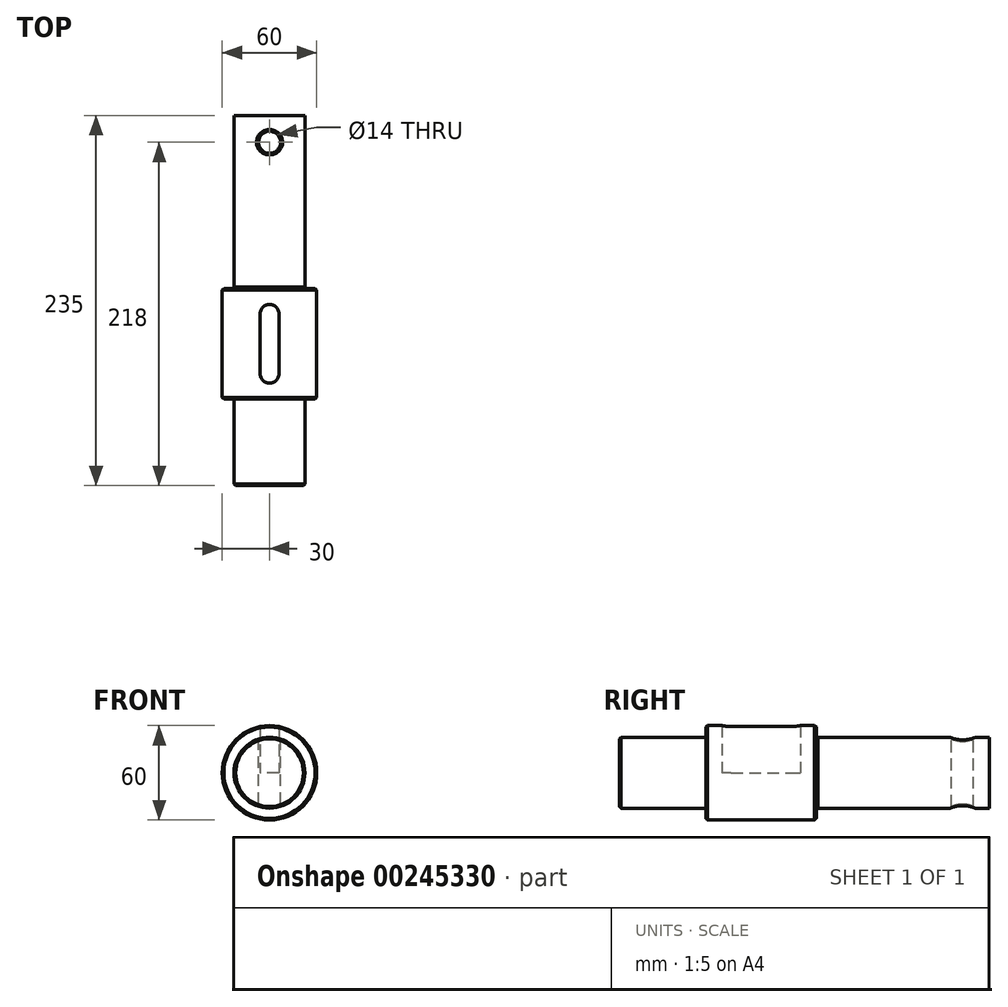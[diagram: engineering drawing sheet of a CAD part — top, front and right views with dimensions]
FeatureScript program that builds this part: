
annotation { "Feature Type Name" : "Feature", "Feature Type Description" : "" }
export const myFeature = defineFeature(function(context is Context, id is Id, definition is map)
    precondition{}
    {
        {
            var Q0;
            Q0=qCreatedBy(makeId("Front.planeOp"),FACE);
            var sketch = newSketch(context, id + "F0", { "sketchPlane" : qUnion([Q0])});
            skCircle(sketch, "E0", {"center": v(0, 0) * mm, "radius": 22.5 * mm});
            skSolve(sketch);
        }
        {
            var Q0;
            Q0 = qSketchRegion(id + "F0", true);
            extrude(context, id + "F1", {"entities" : qUnion([Q0]), "depth" : 110 * mm, "offsetDistance" : 25 * mm});
        }
        {
            var Q0;
            Q0=qCreatedBy(makeId("Top.planeOp"),FACE);
            var sketch = newSketch(context, id + "F2", { "sketchPlane" : qUnion([Q0])});
            skCircle(sketch, "E1", {"center": v(0, -17) * mm, "radius": 7 * mm});
            skSolve(sketch);
        }
        {
            var Q0;
            Q0 = qSketchRegion(id + "F2", true);
            extrude(context, id + "F3", {"entities" : qUnion([Q0]), "operationType" : NewBodyOperationType.REMOVE, "endBound" : BoundingType.THROUGH_ALL, "oppositeDirection" : true, "depth" : 25 * mm, "offsetDistance" : 25 * mm, "hasSecondDirection" : true, "secondDirectionBound" : SecondDirectionBoundingType.THROUGH_ALL, "secondDirectionOppositeDirection" : false, "secondDirectionDepth" : 25 * mm});
        }
        {
            var Q0;
            Q0=makeQuery(id+"F3.boolean.opBoolean","INTERSECT",EDGE,{"disambiguationData":[OD(0.0)],"derivedFrom":[makeQuery(id+"F1.opExtrude","SWEPT_FACE",FACE,{"disambiguationData":[OSD([sQuery(id+"F0.wireOp",EDGE,"E0")])]}),makeQuery(id+"F3.opExtrude","SWEPT_FACE",FACE,{"disambiguationData":[OSD([sQuery(id+"F2.wireOp",EDGE,"E1")])]})]});
            var Q1;
            Q1=makeQuery(id+"F3.boolean.opBoolean","INTERSECT",EDGE,{"disambiguationData":[OD(1.0)],"derivedFrom":[makeQuery(id+"F1.opExtrude","SWEPT_FACE",FACE,{"disambiguationData":[OSD([sQuery(id+"F0.wireOp",EDGE,"E0")])]}),makeQuery(id+"F3.opExtrude","SWEPT_FACE",FACE,{"disambiguationData":[OSD([sQuery(id+"F2.wireOp",EDGE,"E1")])]})]});
            var Q2;
            Q2=makeQuery(id+"FgVqdPoODl7SCyA_1.boolean.opBoolean","INTERSECT",EDGE,{"disambiguationData":[OD(1.0)],"derivedFrom":[makeQuery(id+"F1.opExtrude","SWEPT_FACE",FACE,{"disambiguationData":[OSD([sQuery(id+"F0.wireOp",EDGE,"E0")])]}),makeQuery(id+"FgVqdPoODl7SCyA_1.opExtrude","SWEPT_FACE",FACE,{"disambiguationData":[OSD([sQuery(id+"FY2ivZKtXJa3WG1_1.wireOp",EDGE,"Hc0Fqwav-KuhF-CdOD-GJRH-0QC76LvEiqeI.top")])]})]});
            var Q3;
            Q3=makeQuery(id+"FgVqdPoODl7SCyA_1.boolean.opBoolean","INTERSECT",EDGE,{"disambiguationData":[OD(1.0)],"derivedFrom":[makeQuery(id+"F1.opExtrude","SWEPT_FACE",FACE,{"disambiguationData":[OSD([sQuery(id+"F0.wireOp",EDGE,"E0")])]}),makeQuery(id+"FgVqdPoODl7SCyA_1.opExtrude","SWEPT_FACE",FACE,{"disambiguationData":[OSD([sQuery(id+"FY2ivZKtXJa3WG1_1.wireOp",EDGE,"Hc0Fqwav-KuhF-CdOD-GJRH-0QC76LvEiqeI.bottom")])]})]});
            var Q4;
            Q4=makeQuery(id+"FgVqdPoODl7SCyA_1.boolean.opBoolean","INTERSECT",EDGE,{"disambiguationData":[OD(1.0)],"derivedFrom":[makeQuery(id+"F1.opExtrude","SWEPT_FACE",FACE,{"disambiguationData":[OSD([sQuery(id+"F0.wireOp",EDGE,"E0")])]}),makeQuery(id+"FgVqdPoODl7SCyA_1.opExtrude","CAP_FACE",FACE,{"disambiguationData":[OSD([sQuery(id+"FY2ivZKtXJa3WG1_1.wireOp",EDGE,"Hc0Fqwav-KuhF-CdOD-GJRH-0QC76LvEiqeI.bottom"),sQuery(id+"FY2ivZKtXJa3WG1_1.wireOp",EDGE,"Hc0Fqwav-KuhF-CdOD-GJRH-0QC76LvEiqeI.top"),sQuery(id+"FY2ivZKtXJa3WG1_1.wireOp",EDGE,"Hc0Fqwav-KuhF-CdOD-GJRH-0QC76LvEiqeI.left"),sQuery(id+"FY2ivZKtXJa3WG1_1.wireOp",EDGE,"Hc0Fqwav-KuhF-CdOD-GJRH-0QC76LvEiqeI.right")])],"isStart":false})]});
            var Q5;
            Q5=makeQuery(id+"FgVqdPoODl7SCyA_1.boolean.opBoolean","COPY",EDGE,{"derivedFrom":makeQuery(id+"FgVqdPoODl7SCyA_1.opExtrude","CAP_EDGE",EDGE,{"disambiguationData":[OSD([sQuery(id+"FY2ivZKtXJa3WG1_1.wireOp",EDGE,"Hc0Fqwav-KuhF-CdOD-GJRH-0QC76LvEiqeI.bottom")])],"isStart":true})});
            var Q6;
            Q6=makeQuery(id+"FgVqdPoODl7SCyA_1.boolean.opBoolean","COPY",EDGE,{"derivedFrom":makeQuery(id+"FgVqdPoODl7SCyA_1.opExtrude","CAP_EDGE",EDGE,{"disambiguationData":[OSD([sQuery(id+"FY2ivZKtXJa3WG1_1.wireOp",EDGE,"Hc0Fqwav-KuhF-CdOD-GJRH-0QC76LvEiqeI.top")])],"isStart":true})});
            var Q7;
            Q7=makeQuery(id+"FgVqdPoODl7SCyA_1.boolean.opBoolean","INTERSECT",EDGE,{"disambiguationData":[OD(0.0)],"derivedFrom":[makeQuery(id+"F1.opExtrude","SWEPT_FACE",FACE,{"disambiguationData":[OSD([sQuery(id+"F0.wireOp",EDGE,"E0")])]}),makeQuery(id+"FgVqdPoODl7SCyA_1.opExtrude","SWEPT_FACE",FACE,{"disambiguationData":[OSD([sQuery(id+"FY2ivZKtXJa3WG1_1.wireOp",EDGE,"Hc0Fqwav-KuhF-CdOD-GJRH-0QC76LvEiqeI.top")])]})]});
            var Q8;
            Q8=makeQuery(id+"FgVqdPoODl7SCyA_1.boolean.opBoolean","INTERSECT",EDGE,{"disambiguationData":[OD(0.0)],"derivedFrom":[makeQuery(id+"F1.opExtrude","SWEPT_FACE",FACE,{"disambiguationData":[OSD([sQuery(id+"F0.wireOp",EDGE,"E0")])]}),makeQuery(id+"FgVqdPoODl7SCyA_1.opExtrude","SWEPT_FACE",FACE,{"disambiguationData":[OSD([sQuery(id+"FY2ivZKtXJa3WG1_1.wireOp",EDGE,"Hc0Fqwav-KuhF-CdOD-GJRH-0QC76LvEiqeI.bottom")])]})]});
            var Q9;
            Q9=makeQuery(id+"FgVqdPoODl7SCyA_1.boolean.opBoolean","INTERSECT",EDGE,{"disambiguationData":[OD(0.0)],"derivedFrom":[makeQuery(id+"F1.opExtrude","SWEPT_FACE",FACE,{"disambiguationData":[OSD([sQuery(id+"F0.wireOp",EDGE,"E0")])]}),makeQuery(id+"FgVqdPoODl7SCyA_1.opExtrude","CAP_FACE",FACE,{"disambiguationData":[OSD([sQuery(id+"FY2ivZKtXJa3WG1_1.wireOp",EDGE,"Hc0Fqwav-KuhF-CdOD-GJRH-0QC76LvEiqeI.bottom"),sQuery(id+"FY2ivZKtXJa3WG1_1.wireOp",EDGE,"Hc0Fqwav-KuhF-CdOD-GJRH-0QC76LvEiqeI.top"),sQuery(id+"FY2ivZKtXJa3WG1_1.wireOp",EDGE,"Hc0Fqwav-KuhF-CdOD-GJRH-0QC76LvEiqeI.left"),sQuery(id+"FY2ivZKtXJa3WG1_1.wireOp",EDGE,"Hc0Fqwav-KuhF-CdOD-GJRH-0QC76LvEiqeI.right")])],"isStart":false})]});
            chamfer(context, id + "F4", {"entities" : qUnion([Q0, Q1, Q2, Q3, Q4, Q5, Q6, Q7, Q8, Q9]), "width" : 1 * mm, "tangentPropagation" : true});
        }
        {
            var Q0;
            Q0=makeQuery(id+"F1.opExtrude","CAP_EDGE",EDGE,{"disambiguationData":[OSD([sQuery(id+"F0.wireOp",EDGE,"E0")])],"isStart":false});
            chamfer(context, id + "F5", {"entities" : qUnion([Q0]), "width" : 1 * mm, "tangentPropagation" : true});
        }
        {
            var Q0;
            Q0=makeQuery(id+"F1.opExtrude","CAP_FACE",FACE,{"disambiguationData":[OSD([sQuery(id+"F0.wireOp",EDGE,"E0")])],"isStart":false});
            var sketch = newSketch(context, id + "F6", { "sketchPlane" : qUnion([Q0])});
            skCircle(sketch, "E2", {"center": v(0, 0) * mm, "radius": 30 * mm});
            skSolve(sketch);
        }
        {
            var Q0;
            Q0 = qSketchRegion(id + "F6", true);
            extrude(context, id + "F7", {"entities" : qUnion([Q0]), "operationType" : NewBodyOperationType.ADD, "depth" : 70 * mm, "offsetDistance" : 25 * mm});
        }
        {
            var Q0;
            Q0=makeQuery(id+"F7.opExtrude","CAP_FACE",FACE,{"disambiguationData":[OSD([sQuery(id+"F6.wireOp",EDGE,"E2")])],"isStart":false});
            var sketch = newSketch(context, id + "F8", { "sketchPlane" : qUnion([Q0])});
            skCircle(sketch, "E3", {"center": v(0, 0) * mm, "radius": 22.5 * mm});
            skSolve(sketch);
        }
        {
            var Q0;
            Q0 = qSketchRegion(id + "F8", true);
            extrude(context, id + "F9", {"entities" : qUnion([Q0]), "operationType" : NewBodyOperationType.ADD, "depth" : 55 * mm, "offsetDistance" : 25 * mm});
        }
        {
            var Q0;
            Q0=makeQuery(id+"F9.opExtrude","CAP_EDGE",EDGE,{"disambiguationData":[OSD([sQuery(id+"F8.wireOp",EDGE,"E3")])],"isStart":false});
            var Q1;
            Q1=makeQuery(id+"F7.opExtrude","CAP_EDGE",EDGE,{"disambiguationData":[OSD([sQuery(id+"F6.wireOp",EDGE,"E2")])],"isStart":false});
            var Q2;
            Q2=makeQuery(id+"F7.opExtrude","CAP_EDGE",EDGE,{"disambiguationData":[OSD([sQuery(id+"F6.wireOp",EDGE,"E2")])],"isStart":true});
            chamfer(context, id + "F10", {"entities" : qUnion([Q0, Q1, Q2]), "width" : 1 * mm, "tangentPropagation" : true});
        }
        {
            var Q0;
            Q0=qCreatedBy(makeId("Top.planeOp"),FACE);
            var sketch = newSketch(context, id + "F11", { "sketchPlane" : qUnion([Q0])});
            skLineSegment(sketch, "E4.bottom", {"start": v(0, -170) * mm, "end": v(0, -170) * mm});
            skLineSegment(sketch, "E4.top", {"start": v(0, -120) * mm, "end": v(0, -120) * mm});
            skLineSegment(sketch, "E4.left", {"start": v(6, -164) * mm, "end": v(6, -126) * mm});
            skLineSegment(sketch, "E4.right", {"start": v(-6, -164) * mm, "end": v(-6, -126) * mm});
            skPoint(sketch, "E4.middle", {"position": v(0, -145) * mm});
            skPoint(sketch, "E5.visualSharp", {"position": v(-6, -120) * mm});
            skArc(sketch, "E5.filletArc", {"start": v(0, -120) * mm, "mid": v(-4.24, -121.76) * mm, "end": v(-6, -126) * mm});
            skPoint(sketch, "E6.visualSharp", {"position": v(6, -120) * mm});
            skArc(sketch, "E6.filletArc", {"start": v(6, -126) * mm, "mid": v(4.24, -121.76) * mm, "end": v(0, -120) * mm});
            skPoint(sketch, "E7.visualSharp", {"position": v(-6, -170) * mm});
            skArc(sketch, "E7.filletArc", {"start": v(-6, -164) * mm, "mid": v(-4.24, -168.24) * mm, "end": v(0, -170) * mm});
            skPoint(sketch, "E8.visualSharp", {"position": v(6, -170) * mm});
            skArc(sketch, "E8.filletArc", {"start": v(0, -170) * mm, "mid": v(4.24, -168.24) * mm, "end": v(6, -164) * mm});
            skSolve(sketch);
        }
        {
            var Q0;
            Q0 = qSketchRegion(id + "F11", true);
            extrude(context, id + "F12", {"entities" : qUnion([Q0]), "operationType" : NewBodyOperationType.REMOVE, "depth" : 32 * mm, "offsetDistance" : 25 * mm});
        }
    });
